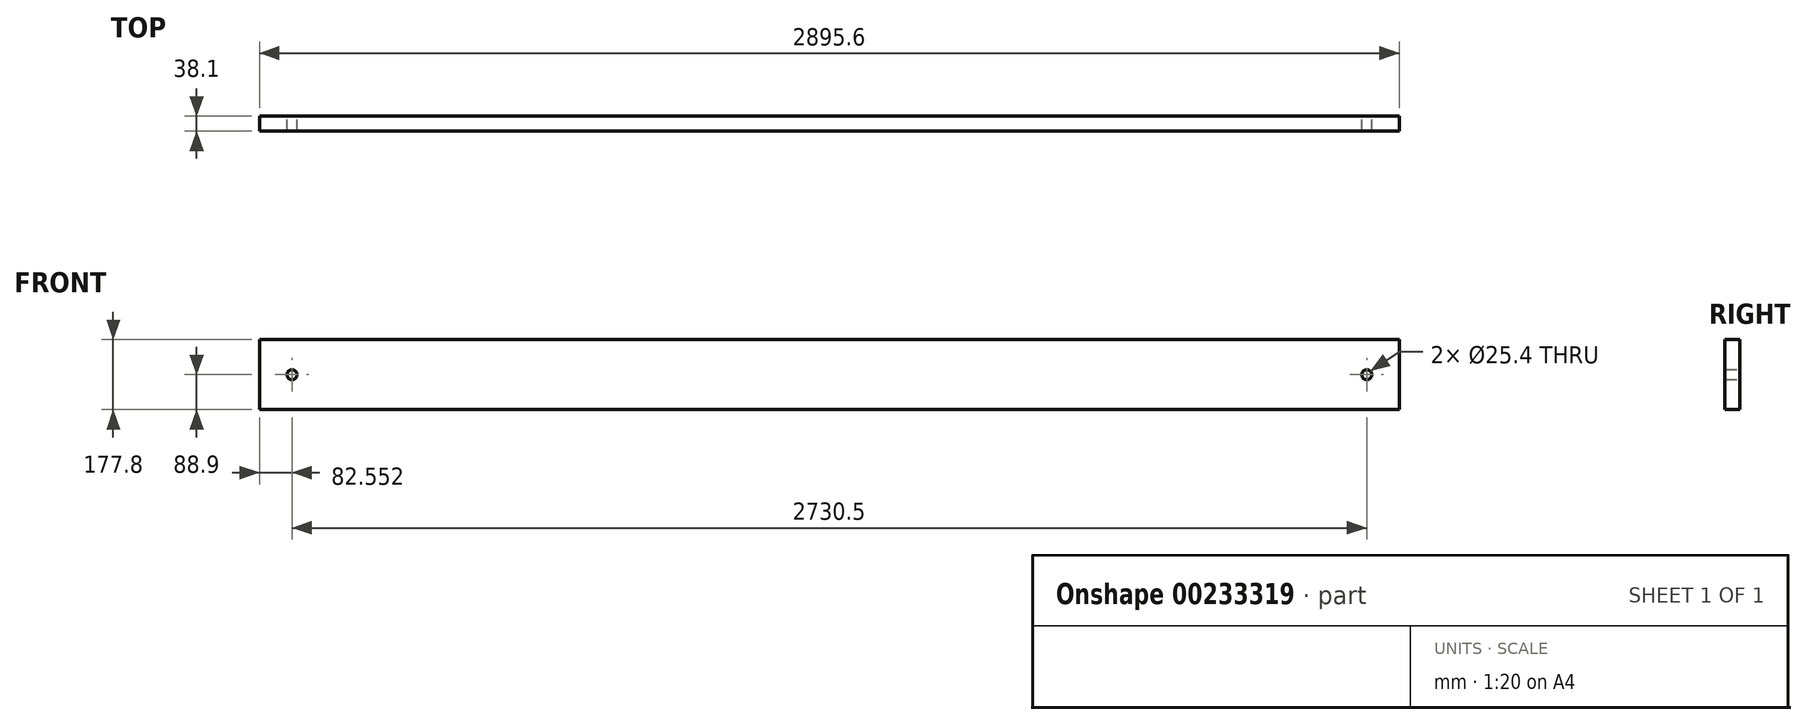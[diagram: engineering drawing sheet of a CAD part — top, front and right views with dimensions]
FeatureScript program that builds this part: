
annotation { "Feature Type Name" : "Feature", "Feature Type Description" : "" }
export const myFeature = defineFeature(function(context is Context, id is Id, definition is map)
    precondition{}
    {
        {
            var Q0;
            Q0=qCreatedBy(makeId("Front.planeOp"),FACE);
            var sketch = newSketch(context, id + "F0", { "sketchPlane" : qUnion([Q0])});
            skLineSegment(sketch, "E0.bottom", {"start": v(-180.29, 88.9) * mm, "end": v(2715.31, 88.9) * mm});
            skLineSegment(sketch, "E0.top", {"start": v(-180.29, -88.9) * mm, "end": v(2715.31, -88.9) * mm});
            skLineSegment(sketch, "E0.left", {"start": v(-180.29, 88.9) * mm, "end": v(-180.29, -88.9) * mm});
            skLineSegment(sketch, "E0.right", {"start": v(2715.31, 88.9) * mm, "end": v(2715.31, -88.9) * mm});
            skCircle(sketch, "E1", {"center": v(-97.74, 0) * mm, "radius": 12.7 * mm});
            skCircle(sketch, "E2", {"center": v(2632.76, 0) * mm, "radius": 12.7 * mm});
            skSolve(sketch);
        }
        {
            var Q0;
            Q0=makeQuery(id+"F0.imprint","IMPRINT",FACE,{"disambiguationData":[TD([[makeQuery(id+"F0.imprint","IMPRINT",EDGE,{"derivedFrom":sQuery(id+"F0.wireOp",EDGE,"E0.bottom")}),-1.0]])]});
            extrude(context, id + "F1", {"entities" : qUnion([Q0]), "depth" : 38.1 * mm});
        }
    });
